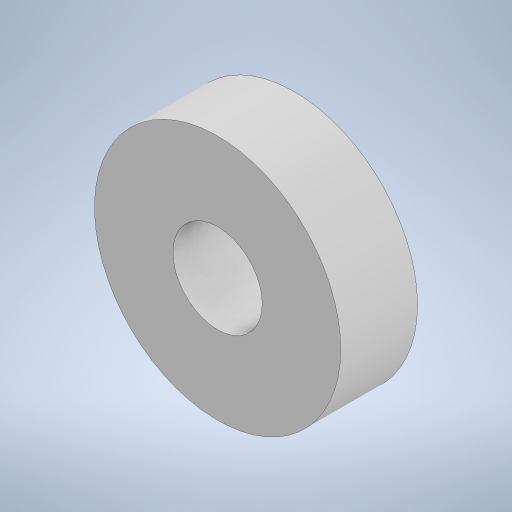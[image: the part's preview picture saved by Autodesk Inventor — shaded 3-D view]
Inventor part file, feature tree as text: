
AUTODESK INVENTOR PART (.ipt)
format: ipt  version: 2023 (Build 270158000, 158)  size: 213,504 bytes
history: native  units: in
note: dims shown in document units (in); Inventor stores cm internally (conversion verified against a paired STEP export)
features: extrude x1, sketch x1
ambient origin geometry x8: Origin, YZ Plane, XZ Plane, XY Plane, X Axis, Y Axis, Z Axis, Center Point
bodies: Solid1 (feature_tree)
feature tree (2):
  extrude  "Extrusion1"  Depth=0.27in
  sketch  "Sketch1"  dims[d0=0.314in d1=0.866in d2=0.27in d3=0.0in]
